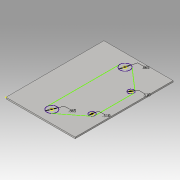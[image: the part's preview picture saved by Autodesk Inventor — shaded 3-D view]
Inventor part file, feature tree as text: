
AUTODESK INVENTOR PART (.ipt)
format: ipt  version: 2016 (Build 200138000, 138)  size: 102,912 bytes
history: native  units: in
note: dims shown in document units (in); Inventor stores cm internally (conversion verified against a paired STEP export)
features: sketch x3, extrude x1, hole x1
ambient origin geometry x8: Origin, YZ Plane, XZ Plane, XY Plane, X Axis, Y Axis, Z Axis, Center Point
bodies: Solid1 (feature_tree)
feature tree (5):
  extrude  "Extrusion1"  Depth=8.5in
  hole  "Hole1"  [1 undecoded]
  sketch  "Sketch5"  dims[d13=1.024in d14=3.11in d15=3.11in d16=1.077in d17=1.077in d18=0.236in d19=0.75in d20=0.375in d21=0.25in d22=0.5635in d23=1.0in d24=0.8108in d25=0.51in d26=0.51in d27=0.865in d28=0.865in d29=2.4818in d30=2.6423in]
  sketch  "Sketch3"  dims[d8=6.0in d9=8.5in]
  sketch  "Sketch4"  dims[d10=0.125in d11=0.0in d12=1.024in]
note: 1 required parameter value undecoded (feature->parameter linkage not recoverable at this tier; creation-order binding heuristic only, values carry confidence <= 0.55)
